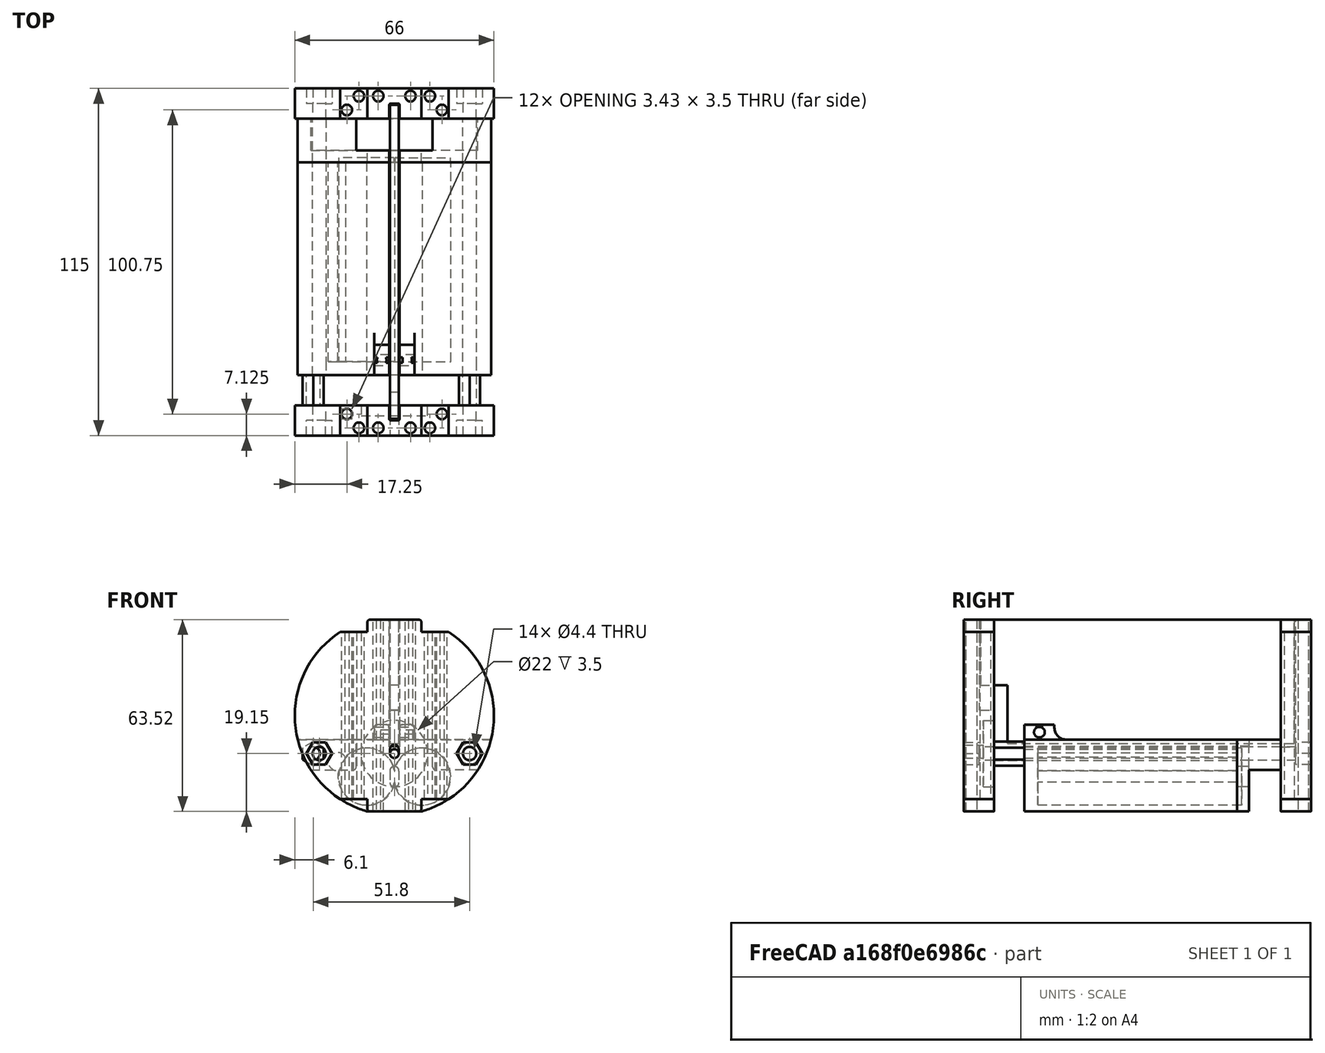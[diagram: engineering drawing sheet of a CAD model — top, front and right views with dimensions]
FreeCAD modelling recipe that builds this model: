
FCSTD DOCUMENT  (FreeCAD 0.19R24276 (Git))
Label: Corte_piezas_DEF_2
License: Creative Commons Attribution-ShareAlike
LicenseURL: http://creativecommons.org/licenses/by-sa/4.0/
objects: Sketcher::SketchObject×22, PartDesign::Pocket×12, PartDesign::Pad×10, TechDraw::DrawViewDimension×9, PartDesign::Fillet×8, PartDesign::Body×7, PartDesign::ShapeBinder×6, PartDesign::Mirrored×5, TechDraw::DrawSVGTemplate×2, TechDraw::DrawViewPart×2, TechDraw::DrawPage×2, Spreadsheet::Sheet×1, PartDesign::MultiTransform×1
note: 101 computed .brp shape members not serialized (recipe doc carries the construction recipe); baked Part::Feature solids carry a one-line shape summary decoded from their .brp

FEATURE [Spreadsheet::Sheet] Spreadsheet  label="Datos"
  cells = A1=Diámetro pila; B1(DiametroPila)=18.5; A2=Tolerancia; B2(tolerancia)=0.4; A3=Largo Pila; B3(largoPila)=65; A4=Separacion; B4(separacion)=1; A5=Grosor tapa; B5(grosortapa)=4.5; A6=Largo Bote; B6(LargoBote)=115; A7= Rosca pasante Diámetro; B7(roscaPasante4)=4; A8=Ancho placa electrónica; B8(anchoPlaca)=3; A9=Diámetro tornillos placa; B9(tornillosParaLaPlaca)=3
FEATURE [Sketcher::SketchObject] Sketch  label="habitaculo_pila_antena"
  FullyConstrained = true
  MapMode = 5
  Placement = pos=(0,0,0) rot=(1,0,0;1.5708rad)
  Support = -> [XZ_Plane]
  expr: Constraints[15] = <<Datos>>.DiametroPila
  expr: Constraints[2] = <<Datos>>.DiametroPila + <<Datos>>.tolerancia
  expr: Constraints[7] = <<Datos>>.tolerancia + <<Datos>>.roscaPasante4
  sketch-geometry (13):
    g0: Circle CenterX=0 CenterY=0 CenterZ=0 NormalX=0 NormalY=0 NormalZ=1 AngleXU=0 Radius=33
    g1: LineSegment StartX=-9.25 StartY=-31.6771 StartZ=0 EndX=9.25 EndY=-31.6771 EndZ=0
    g2: LineSegment StartX=-32.0156 StartY=-8 StartZ=0 EndX=32.0156 EndY=-8 EndZ=0
    g3: ArcOfCircle CenterX=-9.25 CenterY=-20.1771 CenterZ=0 NormalX=0 NormalY=0 NormalZ=1 AngleXU=0 Radius=9.45 StartAngle=0.206102 EndAngle=2.40475
    g4: ArcOfCircle CenterX=9.25 CenterY=-20.1771 CenterZ=0 NormalX=0 NormalY=0 NormalZ=1 AngleXU=0 Radius=9.45 StartAngle=3.3477 EndAngle=9.21868
    g5: Circle CenterX=24.9 CenterY=-12.6 CenterZ=0 NormalX=0 NormalY=0 NormalZ=1 AngleXU=0 Radius=2.2
    g6: ArcOfCircle CenterX=0 CenterY=0 CenterZ=0 NormalX=0 NormalY=0 NormalZ=1 AngleXU=0 Radius=33 StartAngle=3.38646 EndAngle=4.42828
    g7: ArcOfCircle CenterX=0 CenterY=0 CenterZ=0 NormalX=0 NormalY=0 NormalZ=1 AngleXU=0 Radius=33 StartAngle=4.9965 EndAngle=6.03832
    g8: ArcOfCircle CenterX=-18.8935 CenterY=-15.243 CenterZ=0 NormalX=0 NormalY=0 NormalZ=1 AngleXU=0 Radius=3 StartAngle=0.491509 EndAngle=4.84582
    g9: ArcOfCircle CenterX=-9.25 CenterY=-20.1771 CenterZ=0 NormalX=0 NormalY=0 NormalZ=1 AngleXU=0 Radius=9.45 StartAngle=2.93258 EndAngle=6.07708
    g10: Circle CenterX=-24.9 CenterY=-12.6 CenterZ=0 NormalX=0 NormalY=0 NormalZ=1 AngleXU=0 Radius=2.2
    g11: Circle CenterX=0 CenterY=-12.6 CenterZ=0 NormalX=0 NormalY=0 NormalZ=1 AngleXU=0 Radius=1.45
    g12: LineSegment StartX=24.9 StartY=-12.6 StartZ=0 EndX=0 EndY=-12.6 EndZ=0
  constraints (38):
    c: Diameter(g0) = 66
    c: Horizontal(g1)
    c: Diameter(g3) = 18.9
    c: Equal(g3,g4)
    c: Coincident(g4,g9)
    c: Coincident(g4,g3)
    c: Coincident(g0,g-1)
    c: Diameter(g5) = 4.4
    c: Horizontal(g2)
    c: Vertical(g1,g4)
    c: Coincident(g6,g-1)
    c: Coincident(g6,g1)
    c: Coincident(g7,g6)
    c: Coincident(g7,g1)
    c: Symmetric(g4,g3,g-2)
    c: DistanceX(g3,g4) = 18.5
    c: PointOnObject(g1,g0)
    c: DistanceY(g1,g3) = 11.5
    c: DistanceY(g2,g6) = 8
    c: PointOnObject(g6,g0)
    c: Coincident(g2,g6)
    c: Coincident(g7,g2)
    c: Equal(g3,g9)
    c: Coincident(g3,g8)
    c: Coincident(g9,g8)
    c: Coincident(g3,g9)
    c: Radius(g8) = 3
    c: DistanceX(g8,g2) = -13.1222
    c: DistanceY(g8,g2) = 7.24297
    c: Symmetric(g10,g5,g-2)
    c: Equal(g10,g5)
    c: Diameter(g11) = 2.9  'Antena'
    c: Coincident(g12,g5)
    c: Coincident(g12,g11)
    c: Horizontal(g12)
    c: PointOnObject(g11,g-2)
    c: DistanceY(g5,g2) = 4.6
    c: DistanceX(g11,g5) = 24.9
FEATURE [PartDesign::Pad] Pad  label="habitaculo_Pila"
  Direction = (1,1,1)
  Length = 66
  Length2 = 100
  Midplane = true
  Placement = pos=(0,0,0) rot=(1,0,0;1.5708rad)
  Profile = -> Sketch
  Type = 0
  expr: Length = <<Datos>>.largoPila + <<Datos>>.separacion
FEATURE [PartDesign::ShapeBinder] ShapeBinder003
  Placement = pos=(0,-4.5,-1e-15) rot=(0,0,1;0rad)
  TraceSupport = false
FEATURE [Sketcher::SketchObject] Sketch022  label="Sketch_placa"
  ExternalGeometry = -> [ShapeBinder003]
  FullyConstrained = false
  Placement = pos=(0,0,-3.7e-14) rot=(0,0.707107,0.707107;3.14159rad)
  Support = -> [ShapeBinder003]
  expr: Constraints[8] = <<Datos>>.anchoPlaca
  sketch-geometry (4):
    g0: LineSegment StartX=-1.5 StartY=31.7699 StartZ=0 EndX=1.5 EndY=31.7699 EndZ=0
    g1: LineSegment StartX=1.5 StartY=31.7699 StartZ=0 EndX=1.5 EndY=-9.23007 EndZ=0
    g2: LineSegment StartX=1.5 StartY=-9.23007 StartZ=0 EndX=-1.5 EndY=-9.23007 EndZ=0
    g3: LineSegment StartX=-1.5 StartY=-9.23007 StartZ=0 EndX=-1.5 EndY=31.7699 EndZ=0
  constraints (10):
    c: Coincident(g0,g1)
    c: Coincident(g1,g2)
    c: Coincident(g2,g3)
    c: Coincident(g3,g0)
    c: Horizontal(g2)
    c: Vertical(g1)
    c: Vertical(g3)
    c: Symmetric(g0,g0,g-2)
    c: DistanceX(g0,g0) = 3
    c: DistanceY(g1,g1) = 41
FEATURE [PartDesign::Pad] Pad009  label="Placa_electrónica"
  Direction = (1,1,1)
  Length = 104
  Length2 = 100
  Midplane = true
  Placement = pos=(0,-4.5,-1e-15) rot=(0,0,1;0rad)
  Profile = -> Sketch022
  Type = 0
FEATURE [Sketcher::SketchObject] Sketch023
  ExternalGeometry = -> [Pad009]
  FullyConstrained = true
  MapMode = 5
  Placement = pos=(0,-52,5.17e-14) rot=(1,0,0;1.5708rad)
  Support = -> [Pad009]
  sketch-geometry (4):
    g0: LineSegment StartX=-1.5 StartY=-9.23007 StartZ=0 EndX=1.5 EndY=-9.23007 EndZ=0
    g1: LineSegment StartX=1.5 StartY=-9.23007 StartZ=0 EndX=1.5 EndY=10.0699 EndZ=0
    g2: LineSegment StartX=1.5 StartY=10.0699 StartZ=0 EndX=-1.5 EndY=10.0699 EndZ=0
    g3: LineSegment StartX=-1.5 StartY=10.0699 StartZ=0 EndX=-1.5 EndY=-9.23007 EndZ=0
  constraints (11):
    c: Coincident(g0,g1)
    c: Coincident(g1,g2)
    c: Coincident(g2,g3)
    c: Coincident(g3,g0)
    c: Horizontal(g0)
    c: Horizontal(g2)
    c: Vertical(g1)
    c: Vertical(g3)
    c: Coincident(g0,g-3)
    c: PointOnObject(g1,g-4)
    c: DistanceY(g1,g1) = 19.3
FEATURE [PartDesign::Pocket] Pocket011
  BaseFeature = -> Pad009
  Length = 9
  Length2 = 100
  Placement = pos=(0,-4.5,-1e-15) rot=(0,0,1;0rad)
  Profile = -> Sketch023
  Type = 0
FEATURE [PartDesign::Body] Body003  label="Placa_electronica"
  Group = -> [ShapeBinder003,Sketch022,Pad009,Sketch023,Pocket011]
  Origin = -> Origin003
  Tip = -> Pocket011
FEATURE [PartDesign::ShapeBinder] ShapeBinder
  Placement = pos=(0,-4.5,-1e-15) rot=(0,0,1;0rad)
  TraceSupport = false
FEATURE [Sketcher::SketchObject] Sketch024  label="Forma_pasante1"
  ExternalGeometry = -> [ShapeBinder]
  FullyConstrained = true
  MapMode = 5
  Placement = pos=(0,-37.5,-1.19e-14) rot=(1,0,0;1.5708rad)
  Support = -> [ShapeBinder]
  sketch-geometry (8):
    g0: Circle CenterX=24.9 CenterY=-12.6 CenterZ=0 NormalX=0 NormalY=0 NormalZ=1 AngleXU=0 Radius=2.2
    g1: LineSegment StartX=28.3641 StartY=-14.6 StartZ=0 EndX=28.3641 EndY=-10.6 EndZ=0
    g2: LineSegment StartX=28.3641 StartY=-10.6 StartZ=0 EndX=24.9 EndY=-8.6 EndZ=0
    g3: LineSegment StartX=24.9 StartY=-8.6 StartZ=0 EndX=21.4359 EndY=-10.6 EndZ=0
    g4: LineSegment StartX=21.4359 StartY=-10.6 StartZ=0 EndX=21.4359 EndY=-14.6 EndZ=0
    g5: LineSegment StartX=21.4359 StartY=-14.6 StartZ=0 EndX=24.9 EndY=-16.6 EndZ=0
    g6: LineSegment StartX=24.9 StartY=-16.6 StartZ=0 EndX=28.3641 EndY=-14.6 EndZ=0
    g7: Circle CenterX=24.9 CenterY=-12.6 CenterZ=0 NormalX=0 NormalY=0 NormalZ=1 AngleXU=0 Radius=4
  constraints (18):
    c: Coincident(g0,g-3)
    c: Equal(g0,g-3)
    c: Coincident(g1,g2)
    c: Coincident(g2,g3)
    c: Coincident(g3,g4)
    c: Coincident(g4,g5)
    c: Coincident(g5,g6)
    c: Coincident(g6,g1)
    c: Equal(g1, g2-g6) x5
    c: PointOnObject(g1,g7)
    c: PointOnObject(g2,g7)
    c: PointOnObject(g3,g7)
    c: PointOnObject(g4,g7)
    c: PointOnObject(g5,g7)
    c: PointOnObject(g6,g7)
    c: Coincident(g7,g0)
    c: Vertical(g1)
    c: Distance(g2) = 4
FEATURE [PartDesign::Pad] Pad010
  Direction = (1,1,1)
  Length = 10
  Length2 = 100
  Placement = pos=(0,-4.5,-1e-15) rot=(0,0,1;0rad)
  Profile = -> Sketch024
  Type = 0
FEATURE [PartDesign::Body] Body004  label="Pasante1"
  Group = -> [ShapeBinder,Sketch024,Pad010]
  Origin = -> Origin004
  Tip = -> Pad010
FEATURE [PartDesign::ShapeBinder] ShapeBinder004
  Placement = pos=(0,-10,-2.2e-15) rot=(0,0,1;0rad)
  Support = -> [Pad010]
  TraceSupport = false
FEATURE [Sketcher::SketchObject] Sketch025
  ExternalGeometry = -> [ShapeBinder004]
  FullyConstrained = true
  MapMode = 5
  Placement = pos=(0,-47.5,-2.43e-14) rot=(1,0,0;1.5708rad)
  Support = -> [ShapeBinder004]
  sketch-geometry (8):
    g0: Circle CenterX=24.9 CenterY=-12.6 CenterZ=0 NormalX=0 NormalY=0 NormalZ=1 AngleXU=0 Radius=2.2
    g1: LineSegment StartX=28.3641 StartY=-10.6 StartZ=0 EndX=24.9 EndY=-8.6 EndZ=0
    g2: LineSegment StartX=24.9 StartY=-8.6 StartZ=0 EndX=21.4359 EndY=-10.6 EndZ=0
    g3: LineSegment StartX=21.4359 StartY=-10.6 StartZ=0 EndX=21.4359 EndY=-14.6 EndZ=0
    g4: LineSegment StartX=21.4359 StartY=-14.6 StartZ=0 EndX=24.9 EndY=-16.6 EndZ=0
    g5: LineSegment StartX=24.9 StartY=-16.6 StartZ=0 EndX=28.3641 EndY=-14.6 EndZ=0
    g6: LineSegment StartX=28.3641 StartY=-14.6 StartZ=0 EndX=28.3641 EndY=-10.6 EndZ=0
    g7: Circle CenterX=24.9 CenterY=-12.6 CenterZ=0 NormalX=0 NormalY=0 NormalZ=1 AngleXU=0 Radius=4
  constraints (17):
    c: Coincident(g0,g-5)
    c: PointOnObject(g-4,g0)
    c: Coincident(g1,g2)
    c: Coincident(g2,g3)
    c: Coincident(g3,g4)
    c: Coincident(g4,g5)
    c: Coincident(g5,g6)
    c: Coincident(g6,g1)
    c: Equal(g1, g2-g6) x5
    c: PointOnObject(g1,g7)
    c: PointOnObject(g2,g7)
    c: PointOnObject(g3,g7)
    c: PointOnObject(g4,g7)
    c: PointOnObject(g5,g7)
    c: PointOnObject(g6,g7)
    c: Coincident(g7,g0)
    c: Coincident(g6,g-3)
FEATURE [PartDesign::Pad] Pad011
  Direction = (1,1,1)
  Length = 10
  Length2 = 100
  Placement = pos=(0,-10,-2.2e-15) rot=(0,0,1;0rad)
  Profile = -> Sketch025
  Type = 0
FEATURE [PartDesign::Body] Body005  label="Pasante2"
  Group = -> [ShapeBinder004,Sketch025,Pad011]
  Origin = -> Origin005
  Placement = pos=(-51.8,10,1.8e-15) rot=(0,0,1;0rad)
  Tip = -> Pad011
FEATURE [PartDesign::ShapeBinder] ShapeBinder005
  Placement = pos=(0,-4.5,-1e-15) rot=(0,0,1;0rad)
  TraceSupport = false
FEATURE [Sketcher::SketchObject] Sketch026
  ExternalGeometry = -> [ShapeBinder005]
  FullyConstrained = true
  Placement = pos=(0,-47.5,0) rot=(1,0,0;1.5708rad)
  Support = -> [ShapeBinder005]
  sketch-geometry (26):
    g0: ArcOfCircle CenterX=0 CenterY=0 CenterZ=0 NormalX=0 NormalY=0 NormalZ=1 AngleXU=0 Radius=33 StartAngle=5.28932 EndAngle=7.27705
    g1: LineSegment StartX=-9 StartY=-31.749 StartZ=0 EndX=9 EndY=-31.749 EndZ=0
    g2: LineSegment StartX=-9 StartY=31.749 StartZ=0 EndX=9 EndY=31.749 EndZ=0
    g3: ArcOfCircle CenterX=0 CenterY=0 CenterZ=0 NormalX=0 NormalY=0 NormalZ=1 AngleXU=0 Radius=33 StartAngle=2.14773 EndAngle=4.13546
    g4: ArcOfCircle CenterX=0 CenterY=-12.6 CenterZ=0 NormalX=0 NormalY=0 NormalZ=1 AngleXU=0 Radius=1.45 StartAngle=3.14159 EndAngle=6.28319
    g5: ArcOfCircle CenterX=1e-16 CenterY=-11.15 CenterZ=0 NormalX=0 NormalY=0 NormalZ=1 AngleXU=0 Radius=1.45 StartAngle=0 EndAngle=3.14159
    g6: LineSegment StartX=1.45 StartY=-12.6 StartZ=0 EndX=1.45 EndY=-11.15 EndZ=0
    g7: LineSegment StartX=-1.45 StartY=-12.6 StartZ=0 EndX=-1.45 EndY=-11.15 EndZ=0
    g8: LineSegment StartX=-18 StartY=27.6586 StartZ=0 EndX=-18 EndY=-27.6586 EndZ=0
    g9: LineSegment StartX=18 StartY=27.6586 StartZ=0 EndX=18 EndY=-27.6586 EndZ=0
    g10: LineSegment StartX=27.0362 StartY=-16.3 StartZ=0 EndX=29.1724 EndY=-12.6 EndZ=0
    g11: LineSegment StartX=29.1724 StartY=-12.6 StartZ=0 EndX=27.0362 EndY=-8.9 EndZ=0
    g12: LineSegment StartX=27.0362 StartY=-8.9 StartZ=0 EndX=22.7638 EndY=-8.9 EndZ=0
    g13: LineSegment StartX=22.7638 StartY=-8.9 StartZ=0 EndX=20.6276 EndY=-12.6 EndZ=0
    g14: LineSegment StartX=20.6276 StartY=-12.6 StartZ=0 EndX=22.7638 EndY=-16.3 EndZ=0
    g15: LineSegment StartX=22.7638 StartY=-16.3 StartZ=0 EndX=27.0362 EndY=-16.3 EndZ=0
    g16: Circle CenterX=24.9 CenterY=-12.6 CenterZ=0 NormalX=0 NormalY=0 NormalZ=1 AngleXU=0 Radius=4.27239
    g17: LineSegment StartX=22.7638 StartY=-8.9 StartZ=0 EndX=29.1724 EndY=-12.6 EndZ=0
    g18: LineSegment StartX=-18 StartY=27.6586 StartZ=0 EndX=-9 EndY=27.6586 EndZ=0
    g19: LineSegment StartX=-9 StartY=31.749 StartZ=0 EndX=-9 EndY=27.6586 EndZ=0
    g20: LineSegment StartX=-18 StartY=-27.6586 StartZ=0 EndX=-9 EndY=-27.6586 EndZ=0
    g21: LineSegment StartX=-9 StartY=-31.749 StartZ=0 EndX=-9 EndY=-27.6586 EndZ=0
    g22: LineSegment StartX=9 StartY=31.749 StartZ=0 EndX=9 EndY=27.6586 EndZ=0
    g23: LineSegment StartX=18 StartY=27.6586 StartZ=0 EndX=9 EndY=27.6586 EndZ=0
    g24: LineSegment StartX=9 StartY=-31.749 StartZ=0 EndX=9 EndY=-27.6586 EndZ=0
    g25: LineSegment StartX=18 StartY=-27.6586 StartZ=0 EndX=9 EndY=-27.6586 EndZ=0
  constraints (65):
    c: Coincident(g0,g-1)
    c: Coincident(g1,g-4)
    c: PointOnObject(g2,g0)
    c: Horizontal(g2)
    c: Equal(g0,g3)
    c: Coincident(g0,g3)
    c: Tangent(g4,g7) = 1.5708
    c: Tangent(g4,g6) = -1.5708
    c: Tangent(g6,g5) = -1.5708
    c: Tangent(g7,g5) = 1.5708
    c: Vertical(g6)
    c: Equal(g4,g5)
    c: Coincident(g4,g-6)
    c: PointOnObject(g4,g-6)
    c: PointOnObject(g5,g-6)
    c: Vertical(g8)
    c: Vertical(g9)
    c: Coincident(g10,g11)
    c: Coincident(g11,g12)
    c: Coincident(g12,g13)
    c: Coincident(g13,g14)
    c: Coincident(g14,g15)
    c: Coincident(g15,g10)
    c: Equal(g10, g11-g15) x5
    c: PointOnObject(g10,g16)
    c: PointOnObject(g11,g16)
    c: PointOnObject(g12,g16)
    c: PointOnObject(g13,g16)
    c: PointOnObject(g14,g16)
    c: PointOnObject(g15,g16)
    c: Coincident(g16,g-7)
    c: Coincident(g17,g12)
    c: Coincident(g17,g10)
    c: Distance(g17) = 7.4
    c: Horizontal(g15)
    c: Coincident(g19,g2)
    c: Coincident(g19,g18)
    c: Vertical(g19)
    c: Horizontal(g18)
    c: Coincident(g3,g8)
    c: Coincident(g20,g8)
    c: Coincident(g21,g1)
    c: Coincident(g21,g20)
    c: Vertical(g21)
    c: Horizontal(g20)
    c: Coincident(g3,g8)
    c: Vertical(g22)
    c: Coincident(g23,g9)
    c: Coincident(g23,g22)
    c: Coincident(g24,g1)
    c: Vertical(g24)
    c: Coincident(g25,g9)
    c: Coincident(g25,g24)
    c: Horizontal(g25)
    c: Horizontal(g23)
    c: Coincident(g0,g9)
    c: Coincident(g0,g9)
    c: Equal(g23,g18)
    c: Equal(g20,g25)
    c: Equal(g25,g23)
    c: Coincident(g22,g2)
    c: Coincident(g18,g3)
    c: PointOnObject(g0,g-3)
    c: Coincident(g1,g-3)
    c: DistanceX(g23,g23) = 9
FEATURE [PartDesign::Pad] Pad012  label="Cuerpo_principal"
  Direction = (1,1,1)
  Length = 10
  Length2 = 100
  Placement = pos=(0,-4.5,-1e-15) rot=(0,0,1;0rad)
  Profile = -> Sketch026
  Type = 0
FEATURE [Sketcher::SketchObject] Sketch027
  ExternalGeometry = -> [Pad012]
  FullyConstrained = true
  MapMode = 5
  Placement = pos=(0,-4.5,31.749) rot=(0,0,1;0rad)
  Support = -> [Pad012]
  sketch-geometry (4):
    g0: LineSegment StartX=-1.7 StartY=-48 StartZ=0 EndX=1.7 EndY=-48 EndZ=0
    g1: LineSegment StartX=1.7 StartY=-48 StartZ=0 EndX=1.7 EndY=-43 EndZ=0
    g2: LineSegment StartX=1.7 StartY=-43 StartZ=0 EndX=-1.7 EndY=-43 EndZ=0
    g3: LineSegment StartX=-1.7 StartY=-43 StartZ=0 EndX=-1.7 EndY=-48 EndZ=0
  constraints (11):
    c: Coincident(g0,g1)
    c: Coincident(g1,g2)
    c: Coincident(g2,g3)
    c: Coincident(g3,g0)
    c: Horizontal(g0)
    c: Vertical(g1)
    c: Vertical(g3)
    c: PointOnObject(g1,g-4)
    c: Symmetric(g1,g2,g-2)
    c: DistanceX(g0,g0) = 3.4
    c: DistanceY(g1,g1) = 5
FEATURE [PartDesign::Pocket] Pocket  label="Ranura_placa"
  BaseFeature = -> Pad012
  Length = 30
  Length2 = 100
  Placement = pos=(0,-4.5,-1e-15) rot=(0,0,1;0rad)
  Profile = -> Sketch027
  Type = 0
FEATURE [Sketcher::SketchObject] Sketch028  label="SK_agujeros_pasantes_paracaidas"
  ExternalGeometry = -> [Pocket]
  FullyConstrained = true
  MapMode = 5
  Placement = pos=(0,-4.5,31.749) rot=(0,0,1;0rad)
  Support = -> [Pocket]
  sketch-geometry (14):
    g0: LineSegment StartX=-1.7 StartY=-48 StartZ=0 EndX=-9 EndY=-48 EndZ=0
    g1: LineSegment StartX=-1.7 StartY=-48 StartZ=0 EndX=-9 EndY=-53 EndZ=0
    g2: LineSegment StartX=-6.07487 StartY=-48.75 StartZ=0 EndX=-4.62513 EndY=-48.75 EndZ=0
    g3: ArcOfCircle CenterX=-5.35 CenterY=-50.5 CenterZ=0 NormalX=0 NormalY=0 NormalZ=1 AngleXU=0 Radius=1.75 StartAngle=2.35619 EndAngle=7.06858
    g4: LineSegment StartX=-6.07487 StartY=-48.75 StartZ=0 EndX=-6.58744 EndY=-49.2626 EndZ=0
    g5: LineSegment StartX=-4.11256 StartY=-49.2626 StartZ=0 EndX=-4.62513 EndY=-48.75 EndZ=0
    g6: LineSegment StartX=-6.58744 StartY=-49.2626 StartZ=0 EndX=-4.11256 EndY=-49.2626 EndZ=0
    g7: Circle CenterX=-5.35 CenterY=-50.5 CenterZ=0 NormalX=0 NormalY=0 NormalZ=1 AngleXU=0 Radius=1.75
    g8: LineSegment StartX=4.62513 StartY=-48.75 StartZ=0 EndX=6.07487 EndY=-48.75 EndZ=0
    g9: ArcOfCircle CenterX=5.35 CenterY=-50.5 CenterZ=0 NormalX=0 NormalY=0 NormalZ=1 AngleXU=0 Radius=1.75 StartAngle=2.35619 EndAngle=7.06858
    g10: LineSegment StartX=4.62513 StartY=-48.75 StartZ=0 EndX=4.11256 EndY=-49.2626 EndZ=0
    g11: LineSegment StartX=6.58744 StartY=-49.2626 StartZ=0 EndX=6.07487 EndY=-48.75 EndZ=0
    g12: LineSegment StartX=4.11256 StartY=-49.2626 StartZ=0 EndX=6.58744 EndY=-49.2626 EndZ=0
    g13: Circle CenterX=5.35 CenterY=-50.5 CenterZ=0 NormalX=0 NormalY=0 NormalZ=1 AngleXU=0 Radius=1.75
  constraints (33):
    c: Coincident(g0,g-8)
    c: PointOnObject(g0,g-3)
    c: Horizontal(g0)
    c: Coincident(g1,g0)
    c: Coincident(g1,g-3)
    c: Horizontal(g2)
    c: Coincident(g4,g2)
    c: Coincident(g5,g2)
    c: Coincident(g6,g3)
    c: Horizontal(g6)
    c: Tangent(g4,g3) = -1.5708
    c: Tangent(g5,g3) = -1.5708
    c: Angle(g6,g4) = 0.785398
    c: Diameter(g3) = 3.5
    c: Symmetric(g0,g1,g3)
    c: Coincident(g7,g3)
    c: PointOnObject(g3,g7)
    c: Tangent(g7,g2)
    c: Coincident(g3,g6)
    c: Horizontal(g8)
    c: Coincident(g10,g8)
    c: Coincident(g11,g8)
    c: Coincident(g12,g9)
    c: Horizontal(g12)
    c: Tangent(g10,g9) = -1.5708
    c: Tangent(g11,g9) = -1.5708
    c: Angle(g12,g10) = 0.785398
    c: Equal(g3,g9) = 3.5
    c: Coincident(g13,g9)
    c: PointOnObject(g9,g13)
    c: Tangent(g13,g8)
    c: Coincident(g9,g12)
    c: Symmetric(g9,g3,g-2)
FEATURE [PartDesign::Pocket] Pocket012  label="agujeros_pasantes_paracaidas"
  BaseFeature = -> Pocket
  Length = 5
  Length2 = 100
  Placement = pos=(0,-4.5,-1e-15) rot=(0,0,1;0rad)
  Profile = -> Sketch028
  Type = 1
FEATURE [Sketcher::SketchObject] Sketch029
  ExternalGeometry = -> [Pocket012]
  FullyConstrained = true
  MapMode = 5
  Placement = pos=(0,-47.5,8.5e-15) rot=(0,0.707107,0.707107;3.14159rad)
  Support = -> [Pocket012]
  sketch-geometry (2):
    g0: Circle CenterX=0 CenterY=-12.6 CenterZ=0 NormalX=0 NormalY=0 NormalZ=1 AngleXU=0 Radius=11
    g1: Circle CenterX=0 CenterY=-12.6 CenterZ=0 NormalX=0 NormalY=0 NormalZ=1 AngleXU=0 Radius=4
  constraints (4):
    c: Coincident(g0,g-3)
    c: Diameter(g0) = 22
    c: Coincident(g1,g0)
    c: Diameter(g1) = 8
FEATURE [PartDesign::Pocket] Pocket013  label="Arandela_GND"
  BaseFeature = -> Pocket012
  Length = 3.5
  Length2 = 100
  Placement = pos=(0,-4.5,-1e-15) rot=(0,0,1;0rad)
  Profile = -> Sketch029
  Type = 0
FEATURE [Sketcher::SketchObject] Sketch030
  ExternalGeometry = -> [ShapeBinder005]
  FullyConstrained = true
  MapMode = 5
  Placement = pos=(0,-57.5,1.07e-14) rot=(1,0,0;1.5708rad)
  Support = -> [Pocket013]
  sketch-geometry (15):
    g0: LineSegment StartX=27.0362 StartY=-16.3 StartZ=0 EndX=29.1724 EndY=-12.6 EndZ=0
    g1: LineSegment StartX=29.1724 StartY=-12.6 StartZ=0 EndX=27.0362 EndY=-8.9 EndZ=0
    g2: LineSegment StartX=27.0362 StartY=-8.9 StartZ=0 EndX=22.7638 EndY=-8.9 EndZ=0
    g3: LineSegment StartX=22.7638 StartY=-8.9 StartZ=0 EndX=20.6276 EndY=-12.6 EndZ=0
    g4: LineSegment StartX=20.6276 StartY=-12.6 StartZ=0 EndX=22.7638 EndY=-16.3 EndZ=0
    g5: LineSegment StartX=22.7638 StartY=-16.3 StartZ=0 EndX=27.0362 EndY=-16.3 EndZ=0
    g6: Circle CenterX=24.9 CenterY=-12.6 CenterZ=0 NormalX=0 NormalY=0 NormalZ=1 AngleXU=0 Radius=4.27239
    g7: LineSegment StartX=-22.7638 StartY=-16.3 StartZ=0 EndX=-20.6276 EndY=-12.6 EndZ=0
    g8: LineSegment StartX=-20.6276 StartY=-12.6 StartZ=0 EndX=-22.7638 EndY=-8.9 EndZ=0
    g9: LineSegment StartX=-22.7638 StartY=-8.9 StartZ=0 EndX=-27.0362 EndY=-8.9 EndZ=0
    g10: LineSegment StartX=-27.0362 StartY=-8.9 StartZ=0 EndX=-29.1724 EndY=-12.6 EndZ=0
    g11: LineSegment StartX=-29.1724 StartY=-12.6 StartZ=0 EndX=-27.0362 EndY=-16.3 EndZ=0
    g12: LineSegment StartX=-27.0362 StartY=-16.3 StartZ=0 EndX=-22.7638 EndY=-16.3 EndZ=0
    g13: Circle CenterX=-24.9 CenterY=-12.6 CenterZ=0 NormalX=0 NormalY=0 NormalZ=1 AngleXU=0 Radius=4.27239
    g14: LineSegment StartX=22.7638 StartY=-8.9 StartZ=0 EndX=29.1724 EndY=-12.6 EndZ=0
  constraints (34):
    c: Coincident(g0,g1)
    c: Coincident(g1,g2)
    c: Coincident(g2,g3)
    c: Coincident(g3,g4)
    c: Coincident(g4,g5)
    c: Coincident(g5,g0)
    c: Equal(g0, g1-g5) x5
    c: PointOnObject(g0,g6)
    c: PointOnObject(g1,g6)
    c: PointOnObject(g2,g6)
    c: PointOnObject(g3,g6)
    c: PointOnObject(g4,g6)
    c: PointOnObject(g5,g6)
    c: Coincident(g6,g-3)
    c: Coincident(g7,g8)
    c: Coincident(g8,g9)
    c: Coincident(g9,g10)
    c: Coincident(g10,g11)
    c: Coincident(g11,g12)
    c: Coincident(g12,g7)
    c: Equal(g7, g8-g12) x5
    c: PointOnObject(g7,g13)
    c: PointOnObject(g8,g13)
    c: PointOnObject(g9,g13)
    c: PointOnObject(g10,g13)
    c: PointOnObject(g11,g13)
    c: PointOnObject(g12,g13)
    c: Coincident(g13,g-4)
    c: Coincident(g14,g2)
    c: Distance(g14) = 7.4
    c: Horizontal(g5)
    c: Coincident(g14,g0)
    c: Equal(g2,g9)
    c: Horizontal(g12)
FEATURE [PartDesign::Pocket] Pocket014  label="Encastro_tuercas"
  BaseFeature = -> Pocket013
  Length = 5
  Length2 = 100
  Placement = pos=(0,-4.5,-1e-15) rot=(0,0,1;0rad)
  Profile = -> Sketch030
  Type = 0
FEATURE [Sketcher::SketchObject] Sketch031
  ExternalGeometry = -> [Pocket014]
  FullyConstrained = true
  MapMode = 5
  Placement = pos=(0,-52.5,4.51e-14) rot=(1,0,0;1.5708rad)
  Support = -> [Pocket014]
  sketch-geometry (3):
    g0: Circle CenterX=24.9 CenterY=-12.6 CenterZ=0 NormalX=0 NormalY=0 NormalZ=1 AngleXU=0 Radius=4.27239
    g1: Circle CenterX=24.9 CenterY=-12.6 CenterZ=0 NormalX=0 NormalY=0 NormalZ=1 AngleXU=0 Radius=2.2
    g2: Circle CenterX=-24.9 CenterY=-12.6 CenterZ=0 NormalX=0 NormalY=0 NormalZ=1 AngleXU=0 Radius=2.2
  constraints (7):
    c: PointOnObject(g-8,g0)
    c: PointOnObject(g-4,g0)
    c: PointOnObject(g-5,g0)
    c: Coincident(g1,g0)
    c: Diameter(g1) = 4.4
    c: Equal(g1,g2) = 4.4
    c: Symmetric(g2,g1,g-2)
FEATURE [PartDesign::Pocket] Pocket015  label="Agujeros_pasantes_tornillos"
  BaseFeature = -> Pocket014
  Length = 5
  Length2 = 100
  Placement = pos=(0,-4.5,-1e-15) rot=(0,0,1;0rad)
  Profile = -> Sketch031
  Type = 1
FEATURE [Sketcher::SketchObject] Sketch032  label="SK_agujeros_pasantes_paracaidas_2"
  ExternalGeometry = -> [Pocket015]
  FullyConstrained = true
  MapMode = 5
  Placement = pos=(0,-4.5,27.6586) rot=(0,0,1;0rad)
  Support = -> [Pocket015]
  sketch-geometry (16):
    g0: LineSegment StartX=11.0251 StartY=-48.75 StartZ=0 EndX=12.4749 EndY=-48.75 EndZ=0
    g1: ArcOfCircle CenterX=11.75 CenterY=-50.5 CenterZ=0 NormalX=0 NormalY=0 NormalZ=1 AngleXU=0 Radius=1.75 StartAngle=2.35619 EndAngle=7.06858
    g2: LineSegment StartX=11.0251 StartY=-48.75 StartZ=0 EndX=10.5126 EndY=-49.2626 EndZ=0
    g3: LineSegment StartX=12.4749 StartY=-48.75 StartZ=0 EndX=12.9874 EndY=-49.2626 EndZ=0
    g4: LineSegment StartX=10.5126 StartY=-49.2626 StartZ=0 EndX=12.9874 EndY=-49.2626 EndZ=0
    g5: LineSegment StartX=6.07487 StartY=-48.75 StartZ=0 EndX=18 EndY=-48.75 EndZ=0
    g6: LineSegment StartX=13.5 StartY=-43 StartZ=0 EndX=13.5 EndY=-53 EndZ=0
    g7: ArcOfCircle CenterX=11.75 CenterY=-50.5 CenterZ=0 NormalX=0 NormalY=0 NormalZ=1 AngleXU=0 Radius=1.75 StartAngle=1.5708 EndAngle=2.35619
    g8: LineSegment StartX=15.0251 StartY=-44.125 StartZ=0 EndX=16.4749 EndY=-44.125 EndZ=0
    g9: ArcOfCircle CenterX=15.75 CenterY=-45.875 CenterZ=0 NormalX=0 NormalY=0 NormalZ=1 AngleXU=0 Radius=1.75 StartAngle=2.35619 EndAngle=7.06858
    g10: LineSegment StartX=15.0251 StartY=-44.125 StartZ=0 EndX=14.5126 EndY=-44.6376 EndZ=0
    g11: LineSegment StartX=16.4749 StartY=-44.125 StartZ=0 EndX=16.9874 EndY=-44.6376 EndZ=0
    g12: LineSegment StartX=14.5126 StartY=-44.6376 StartZ=0 EndX=16.9874 EndY=-44.6376 EndZ=0
    g13: ArcOfCircle CenterX=15.75 CenterY=-45.875 CenterZ=0 NormalX=0 NormalY=0 NormalZ=1 AngleXU=0 Radius=1.75 StartAngle=1.57079 EndAngle=2.35619
    g14: LineSegment StartX=13.5 StartY=-43 StartZ=0 EndX=18 EndY=-48.75 EndZ=0
    g15: LineSegment StartX=13.5 StartY=-48.75 StartZ=0 EndX=18 EndY=-43 EndZ=0
  constraints (43):
    c: Diameter(g1) = 3.5
    c: Coincident(g1,g4)
    c: Horizontal(g4)
    c: Coincident(g0,g2)
    c: Horizontal(g0)
    c: Coincident(g0,g3)
    c: PointOnObject(g5,g-3)
    c: Horizontal(g5)
    c: PointOnObject(g6,g-5)
    c: Vertical(g6)
    c: Symmetric(g-4,g-6,g6)
    c: Tangent(g1,g2) = -1.5708
    c: Tangent(g3,g1) = 1.5708
    c: Coincident(g4,g1)
    c: Coincident(g7,g1)
    c: Coincident(g7,g1)
    c: Tangent(g0,g7)
    c: Angle(g4,g2) = 0.785398
    c: PointOnObject(g7,g0)
    c: Coincident(g5,g-7)
    c: Diameter(g9) = 3.5
    c: Coincident(g9,g12)
    c: Horizontal(g12)
    c: Coincident(g8,g10)
    c: Horizontal(g8)
    c: Coincident(g8,g11)
    c: Tangent(g9,g10) = -1.5708
    c: Tangent(g11,g9) = 1.5708
    c: Coincident(g12,g9)
    c: Coincident(g13,g9)
    c: Coincident(g13,g9)
    c: Tangent(g8,g13)
    c: Angle(g12,g10) = 0.785398
    c: PointOnObject(g13,g8)
    c: Coincident(g14,g6)
    c: Coincident(g14,g5)
    c: PointOnObject(g9,g14)
    c: PointOnObject(g15,g6)
    c: Coincident(g15,g-4)
    c: PointOnObject(g9,g15)
    c: PointOnObject(g15,g5)
    c: PointOnObject(g0,g5)
    c: Tangent(g1,g6)
FEATURE [PartDesign::Pocket] Pocket016  label="Agujeros_pasantes_paracaidas_2"
  BaseFeature = -> Pocket015
  Length = 5
  Length2 = 100
  Placement = pos=(0,-4.5,-1e-15) rot=(0,0,1;0rad)
  Profile = -> Sketch032
  Type = 1
FEATURE [PartDesign::Mirrored] Mirrored  label="Con_todos_agujeros_pasantes"
  BaseFeature = -> Pocket016
  MirrorPlane = -> Sketch032 [V_Axis]
  Originals = -> [Pocket016]
  Placement = pos=(0,-4.5,-1e-15) rot=(0,0,1;0rad)
FEATURE [PartDesign::Fillet] Fillet
  Base = -> Mirrored [Edge123,Edge109]
  BaseFeature = -> Mirrored
  Placement = pos=(0,-4.5,-1e-15) rot=(0,0,1;0rad)
  Radius = 0.5
  SupportTransform = false
FEATURE [PartDesign::Fillet] Fillet001
  Base = -> Fillet [Edge5,Edge9]
  BaseFeature = -> Fillet
  Placement = pos=(0,-4.5,-1e-15) rot=(0,0,1;0rad)
  Radius = 1
  SupportTransform = false
FEATURE [PartDesign::Fillet] Fillet002
  Base = -> Fillet001 [Edge114,Edge115]
  BaseFeature = -> Fillet001
  Placement = pos=(0,-4.5,-1e-15) rot=(0,0,1;0rad)
  Radius = 1
  SupportTransform = false
FEATURE [PartDesign::Body] Body006  label="LateralA"
  Group = -> [ShapeBinder005,Sketch026,Pad012,Sketch027,Pocket,Sketch028,Pocket012,Sketch029,Pocket013,Sketch030,Pocket014,Sketch031,Pocket015,Sketch032,Pocket016,Mirrored,Fillet,Fillet001,Fillet002]
  Origin = -> Origin006
  Tip = -> Fillet002
FEATURE [PartDesign::ShapeBinder] ShapeBinder006
  Placement = pos=(0,33,7e-15) rot=(0,0,1;0rad)
  TraceSupport = false
FEATURE [Sketcher::SketchObject] Sketch033
  ExternalGeometry = -> [ShapeBinder006]
  FullyConstrained = true
  MapMode = 5
  Placement = pos=(0,33,7e-15) rot=(0,0.707107,0.707107;3.14159rad)
  Support = -> [ShapeBinder006]
  sketch-geometry (10):
    g0: ArcOfCircle CenterX=1.2e-15 CenterY=0 CenterZ=0 NormalX=0 NormalY=0 NormalZ=1 AngleXU=0 Radius=33 StartAngle=4.98862 EndAngle=6.03832
    g1: ArcOfCircle CenterX=1.2e-15 CenterY=0 CenterZ=0 NormalX=0 NormalY=0 NormalZ=1 AngleXU=0 Radius=33 StartAngle=3.38646 EndAngle=4.43616
    g2: LineSegment StartX=-32.0156 StartY=-8 StartZ=0 EndX=32.0156 EndY=-8 EndZ=0
    g3: LineSegment StartX=9 StartY=-31.749 StartZ=0 EndX=-9 EndY=-31.749 EndZ=0
    g4: ArcOfCircle CenterX=0 CenterY=-18.3411 CenterZ=0 NormalX=0 NormalY=0 NormalZ=1 AngleXU=0 Radius=1.5 StartAngle=9e-16 EndAngle=3.14159
    g5: ArcOfCircle CenterX=0 CenterY=-22.1569 CenterZ=0 NormalX=0 NormalY=0 NormalZ=1 AngleXU=0 Radius=1.5 StartAngle=3.14159 EndAngle=6.28319
    g6: LineSegment StartX=-1.5 StartY=-18.3411 StartZ=0 EndX=-1.5 EndY=-22.1569 EndZ=0
    g7: LineSegment StartX=1.5 StartY=-18.3411 StartZ=0 EndX=1.5 EndY=-22.1569 EndZ=0
    g8: Circle CenterX=24.9 CenterY=-12.6 CenterZ=0 NormalX=0 NormalY=0 NormalZ=1 AngleXU=0 Radius=2.2
    g9: Circle CenterX=-24.9 CenterY=-12.6 CenterZ=0 NormalX=0 NormalY=0 NormalZ=1 AngleXU=0 Radius=2.2
  constraints (21):
    c: Coincident(g0,g-3)
    c: Coincident(g0,g-4)
    c: Coincident(g1,g0)
    c: Coincident(g1,g-3)
    c: Coincident(g1,g-4)
    c: Coincident(g2,g1)
    c: Coincident(g2,g0)
    c: Coincident(g3,g0)
    c: Coincident(g3,g1)
    c: Tangent(g4,g7) = 1.5708
    c: Tangent(g4,g6) = -1.5708
    c: Tangent(g6,g5) = -1.5708
    c: Tangent(g7,g5) = 1.5708
    c: Vertical(g6)
    c: Coincident(g4,g-5)
    c: Coincident(g5,g-6)
    c: Diameter(g4) = 3
    c: Coincident(g8,g-8)
    c: Equal(g8,g-7)
    c: Coincident(g9,g-7)
    c: Equal(g9,g-7)
FEATURE [PartDesign::Pad] Pad013  label="tapa_pilas"
  Direction = (1,1,1)
  Length = 4
  Length2 = 100
  Placement = pos=(0,33,7e-15) rot=(0,0,1;0rad)
  Profile = -> Sketch033
  Type = 0
FEATURE [Sketcher::SketchObject] Sketch034
  ExternalGeometry = -> [Pad013]
  FullyConstrained = true
  MapMode = 5
  Placement = pos=(0,37,8.3e-15) rot=(0,0.707107,0.707107;3.14159rad)
  Support = -> [Pad013]
  sketch-geometry (10):
    g0: ArcOfCircle CenterX=0 CenterY=0 CenterZ=0 NormalX=0 NormalY=0 NormalZ=1 AngleXU=0 Radius=33 StartAngle=3.38646 EndAngle=3.71852
    g1: LineSegment StartX=-27.6586 StartY=-18 StartZ=0 EndX=-12.6586 EndY=-18 EndZ=0
    g2: LineSegment StartX=-12.6586 StartY=-18 StartZ=0 EndX=-12.6586 EndY=-8 EndZ=0
    g3: LineSegment StartX=-32.0156 StartY=-8 StartZ=0 EndX=-12.6586 EndY=-8 EndZ=0
    g4: Circle CenterX=-24.9 CenterY=-12.6 CenterZ=0 NormalX=0 NormalY=0 NormalZ=1 AngleXU=0 Radius=2.2
    g5: ArcOfCircle CenterX=-5.1e-15 CenterY=-8.1e-15 CenterZ=0 NormalX=0 NormalY=0 NormalZ=1 AngleXU=0 Radius=33 StartAngle=5.70625 EndAngle=6.03832
    g6: LineSegment StartX=27.6586 StartY=-18 StartZ=0 EndX=12.6586 EndY=-18 EndZ=0
    g7: LineSegment StartX=12.6586 StartY=-18 StartZ=0 EndX=12.6586 EndY=-8 EndZ=0
    g8: LineSegment StartX=32.0156 StartY=-8 StartZ=0 EndX=12.6586 EndY=-8 EndZ=0
    g9: Circle CenterX=24.9 CenterY=-12.6 CenterZ=0 NormalX=0 NormalY=0 NormalZ=1 AngleXU=0 Radius=2.2
  constraints (24):
    c: Coincident(g0,g-1)
    c: Coincident(g0,g-3)
    c: Coincident(g1,g0)
    c: Horizontal(g1)
    c: PointOnObject(g2,g-3)
    c: Vertical(g2)
    c: Coincident(g2,g1)
    c: Coincident(g3,g0)
    c: Coincident(g3,g2)
    c: DistanceY(g2,g2) = 10
    c: DistanceX(g1,g1) = 15
    c: Coincident(g4,g-4)
    c: Equal(g-4,g4)
    c: Coincident(g6,g5)
    c: Coincident(g7,g6)
    c: Coincident(g8,g5)
    c: Coincident(g8,g7)
    c: Symmetric(g7,g2,g-2)
    c: Symmetric(g6,g1,g-2)
    c: Symmetric(g5,g0,g-2)
    c: Symmetric(g9,g4,g-2)
    c: Equal(g9,g4)
    c: Equal(g5,g0)
    c: Symmetric(g5,g0,g-2)
FEATURE [PartDesign::Pad] Pad014
  BaseFeature = -> Pad013
  Direction = (1,1,1)
  Length = 10.5
  Length2 = 100
  Placement = pos=(0,33,7e-15) rot=(0,0,1;0rad)
  Profile = -> Sketch034
  Type = 0
FEATURE [PartDesign::Fillet] Fillet003
  Base = -> Pad014 [Edge51,Edge48]
  BaseFeature = -> Pad014
  Placement = pos=(0,33,7e-15) rot=(0,0,1;0rad)
  Radius = 1
  SupportTransform = false
FEATURE [PartDesign::ShapeBinder] ShapeBinder007
  TraceSupport = false
FEATURE [Sketcher::SketchObject] Sketch035
  ExternalGeometry = -> [ShapeBinder007]
  FullyConstrained = true
  MapMode = 5
  Placement = pos=(0,-47.5,1.04e-14) rot=(0,0.707107,0.707107;3.14159rad)
  Support = -> [ShapeBinder007]
  sketch-geometry (14):
    g0: ArcOfCircle CenterX=0 CenterY=-1.2e-14 CenterZ=0 NormalX=0 NormalY=0 NormalZ=1 AngleXU=0 Radius=33 StartAngle=2.14773 EndAngle=4.13546
    g1: ArcOfCircle CenterX=0 CenterY=-1.2e-14 CenterZ=0 NormalX=0 NormalY=0 NormalZ=1 AngleXU=0 Radius=33 StartAngle=5.28932 EndAngle=7.27705
    g2: LineSegment StartX=-18 StartY=27.6586 StartZ=0 EndX=-9 EndY=27.6586 EndZ=0
    g3: LineSegment StartX=9 StartY=27.6586 StartZ=0 EndX=18 EndY=27.6586 EndZ=0
    g4: LineSegment StartX=-9 StartY=27.6586 StartZ=0 EndX=-9 EndY=31.749 EndZ=0
    g5: LineSegment StartX=9 StartY=27.6586 StartZ=0 EndX=9 EndY=31.749 EndZ=0
    g6: LineSegment StartX=-9 StartY=31.749 StartZ=0 EndX=9 EndY=31.749 EndZ=0
    g7: LineSegment StartX=-9 StartY=-27.6586 StartZ=0 EndX=-9 EndY=-31.749 EndZ=0
    g8: LineSegment StartX=9 StartY=-27.6586 StartZ=0 EndX=9 EndY=-31.749 EndZ=0
    g9: LineSegment StartX=9 StartY=-27.6586 StartZ=0 EndX=18 EndY=-27.6586 EndZ=0
    g10: LineSegment StartX=-18 StartY=-27.6586 StartZ=0 EndX=-9 EndY=-27.6586 EndZ=0
    g11: LineSegment StartX=-9 StartY=-31.749 StartZ=0 EndX=9 EndY=-31.749 EndZ=0
    g12: Circle CenterX=-24.9 CenterY=-12.6 CenterZ=0 NormalX=0 NormalY=0 NormalZ=1 AngleXU=0 Radius=2.2
    g13: Circle CenterX=24.9 CenterY=-12.6 CenterZ=0 NormalX=0 NormalY=0 NormalZ=1 AngleXU=0 Radius=2.2
  constraints (34):
    c: Coincident(g0,g-5)
    c: Coincident(g0,g-7)
    c: Coincident(g1,g0)
    c: Coincident(g1,g-6)
    c: Coincident(g1,g-9)
    c: Coincident(g2,g0)
    c: Coincident(g2,g-5)
    c: Coincident(g3,g-6)
    c: Coincident(g3,g1)
    c: Coincident(g4,g2)
    c: Vertical(g4)
    c: Coincident(g5,g3)
    c: Vertical(g5)
    c: Coincident(g6,g4)
    c: Coincident(g6,g5)
    c: Horizontal(g6)
    c: PointOnObject(g-3,g6)
    c: Coincident(g7,g-7)
    c: Vertical(g7)
    c: Coincident(g8,g-9)
    c: Vertical(g8)
    c: Coincident(g9,g8)
    c: Coincident(g9,g1)
    c: Coincident(g10,g0)
    c: Coincident(g10,g7)
    c: Coincident(g11,g7)
    c: Coincident(g11,g8)
    c: Horizontal(g11)
    c: PointOnObject(g-8,g11)
    c: Coincident(g12,g-10)
    c: Coincident(g13,g-11)
    c: Equal(g12,g13)
    c: Equal(g13,g-11)
    c: Coincident(g0,g-1)
FEATURE [PartDesign::Pad] Pad015
  Direction = (1,1,1)
  Length = 10
  Length2 = 100
  Profile = -> Sketch035
  Reversed = true
  Type = 0
FEATURE [Sketcher::SketchObject] Sketch036
  ExternalGeometry = -> [Pad015]
  FullyConstrained = true
  MapMode = 5
  Placement = pos=(0,-47.5,1.04e-14) rot=(0,0.707107,0.707107;3.14159rad)
  Support = -> [Pad015]
  sketch-geometry (4):
    g0: LineSegment StartX=-1.7 StartY=31.749 StartZ=0 EndX=1.7 EndY=31.749 EndZ=0
    g1: LineSegment StartX=1.7 StartY=31.749 StartZ=0 EndX=1.7 EndY=-10.351 EndZ=0
    g2: LineSegment StartX=1.7 StartY=-10.351 StartZ=0 EndX=-1.7 EndY=-10.351 EndZ=0
    g3: LineSegment StartX=-1.7 StartY=-10.351 StartZ=0 EndX=-1.7 EndY=31.749 EndZ=0
  constraints (11):
    c: Coincident(g0,g1)
    c: Coincident(g1,g2)
    c: Coincident(g2,g3)
    c: Coincident(g3,g0)
    c: Horizontal(g2)
    c: Vertical(g1)
    c: Vertical(g3)
    c: PointOnObject(g0,g-3)
    c: Symmetric(g0,g0,g-2)
    c: DistanceX(g0,g0) = 3.4
    c: DistanceY(g1,g1) = 42.1
FEATURE [PartDesign::Pocket] Pocket017
  BaseFeature = -> Pad015
  Length = 5
  Length2 = 100
  Profile = -> Sketch036
  Type = 0
FEATURE [PartDesign::Mirrored] Mirrored001
  BaseFeature = -> Pocket017
  MirrorPlane = -> Sketch028 [V_Axis]
  Originals = -> [Pocket012]
FEATURE [PartDesign::Mirrored] Mirrored002
  MirrorPlane = -> Sketch032 [V_Axis]
FEATURE [PartDesign::Mirrored] Mirrored003
  MirrorPlane = -> Sketch032 [V_Axis]
FEATURE [PartDesign::MultiTransform] MultiTransform
  BaseFeature = -> Mirrored001
  Originals = -> [Pocket016]
  Transformations = -> [Mirrored002,Mirrored003]
FEATURE [PartDesign::Mirrored] Mirrored004
  BaseFeature = -> MultiTransform
  MirrorPlane = -> Sketch030 [V_Axis]
  Originals = -> [Pocket014]
FEATURE [PartDesign::Fillet] Fillet004
  Base = -> Mirrored004 [Edge85,Edge88]
  BaseFeature = -> Mirrored004
  Radius = 0.5
  SupportTransform = false
FEATURE [PartDesign::Fillet] Fillet005
  Base = -> Fillet004 [Edge9,Edge5,Edge113,Edge114]
  BaseFeature = -> Fillet004
  Radius = 1
  SupportTransform = false
FEATURE [PartDesign::Body] Body009  label="LateralB"
  Group = -> [ShapeBinder007,Sketch035,Pad015,Sketch036,Pocket017,Mirrored001,MultiTransform,Mirrored002,Mirrored003,Mirrored004,Fillet004,Fillet005]
  Origin = -> Origin009
  Placement = pos=(0,0,0) rot=(0,0,1;3.14159rad)
  Tip = -> Fillet005
FEATURE [TechDraw::DrawSVGTemplate] Template
  EditableTexts = Designed_by_Name=Designed by Name; Drawing_number=Drawing number; FC-Date=Date; FC-SC=Scale; FC-SH=Sheet; FC-Title=Title; Subtitle=Subtitle; Weight=Weight
  Height = 210
  Orientation = 1
  Width = 297
FEATURE [TechDraw::DrawSVGTemplate] Template001
  EditableTexts = Designed_by_Name=Designed by Name; Drawing_number=Drawing number; FC-Date=Date; FC-SC=Scale; FC-SH=Sheet; FC-Title=Title; Subtitle=Subtitle; Weight=Weight
  Height = 210
  Orientation = 1
  Width = 297
FEATURE [TechDraw::DrawViewPart] View001
  CoarseView = false
  Direction = (1,0,0)
  Focus = 100
  HardHidden = false
  IsoCount = 0
  IsoHidden = false
  IsoVisible = false
  LockPosition = false
  Perspective = false
  Rotation = 0
  Scale = 2
  ScaleType = 0
  SeamHidden = false
  SeamVisible = true
  SmoothHidden = false
  SmoothVisible = true
  Source = -> [Body003]
  X = 147.843
  XDirection = (0,1,0)
  Y = 132.277
FEATURE [TechDraw::DrawViewDimension] Dimension004
  Arbitrary = false
  ArbitraryTolerances = false
  EqualTolerance = true
  FormatSpec = %.2f
  FormatSpecOverTolerance = %+.2f
  FormatSpecUnderTolerance = %+.2f
  Inverted = false
  LockPosition = false
  MeasureType = 1
  OverTolerance = 0
  References2D = -> [View001]
  Rotation = 0
  ScaleType = 0
  TheoreticalExact = false
  Type = 1
  UnderTolerance = 0
  X = 0
  Y = 53.2239
FEATURE [TechDraw::DrawViewDimension] Dimension005
  Arbitrary = false
  ArbitraryTolerances = false
  EqualTolerance = true
  FormatSpec = %.2f
  FormatSpecOverTolerance = %+.2f
  FormatSpecUnderTolerance = %+.2f
  Inverted = false
  LockPosition = false
  MeasureType = 1
  OverTolerance = 0
  References2D = -> [View001]
  Rotation = 0
  ScaleType = 0
  TheoreticalExact = false
  Type = 2
  UnderTolerance = 0
  X = 113.202
  Y = 0
FEATURE [TechDraw::DrawViewDimension] Dimension006
  Arbitrary = false
  ArbitraryTolerances = false
  EqualTolerance = true
  FormatSpec = %.2f
  FormatSpecOverTolerance = %+.2f
  FormatSpecUnderTolerance = %+.2f
  Inverted = false
  LockPosition = false
  MeasureType = 1
  OverTolerance = 0
  References2D = -> [View001]
  Rotation = 0
  ScaleType = 0
  TheoreticalExact = false
  Type = 1
  UnderTolerance = 0
  X = -119.319
  Y = -43.8728
FEATURE [TechDraw::DrawViewDimension] Dimension007
  Arbitrary = false
  ArbitraryTolerances = false
  EqualTolerance = true
  FormatSpec = %.2f
  FormatSpecOverTolerance = %+.2f
  FormatSpecUnderTolerance = %+.2f
  Inverted = false
  LockPosition = false
  MeasureType = 1
  OverTolerance = 0
  References2D = -> [View001]
  Rotation = 0
  ScaleType = 0
  TheoreticalExact = false
  Type = 2
  UnderTolerance = 0
  X = -125.437
  Y = -17.8207
FEATURE [TechDraw::DrawViewDimension] Dimension008
  Arbitrary = false
  ArbitraryTolerances = false
  EqualTolerance = true
  FormatSpec = %.2f
  FormatSpecOverTolerance = %+.2f
  FormatSpecUnderTolerance = %+.2f
  Inverted = false
  LockPosition = false
  MeasureType = 1
  OverTolerance = 0
  References2D = -> [View001]
  Rotation = 0
  ScaleType = 0
  TheoreticalExact = false
  Type = 2
  UnderTolerance = 0
  X = -125.362
  Y = 19.3
FEATURE [TechDraw::DrawPage] Page001  label="Placa_electrónica_vista"
  KeepUpdated = true
  NextBalloonIndex = 1
  ProjectionType = 0
  Template = -> Template001
  Views = -> [View001,Dimension004,Dimension005,Dimension006,Dimension007,Dimension008]
FEATURE [Sketcher::SketchObject] Sketch037
  ExternalGeometry = -> [Pad]
  FullyConstrained = true
  MapMode = 5
  Placement = pos=(0,-33,-7.3e-15) rot=(1,0,0;1.5708rad)
  Support = -> [Pad]
  sketch-geometry (7):
    g0: ArcOfCircle CenterX=-7e-16 CenterY=2.8e-15 CenterZ=0 NormalX=0 NormalY=0 NormalZ=1 AngleXU=0 Radius=33 StartAngle=3.38646 EndAngle=4.42828
    g1: ArcOfCircle CenterX=-7e-16 CenterY=2.8e-15 CenterZ=0 NormalX=0 NormalY=0 NormalZ=1 AngleXU=0 Radius=33 StartAngle=4.9965 EndAngle=6.03832
    g2: LineSegment StartX=-32.0156 StartY=-8 StartZ=0 EndX=32.0156 EndY=-8 EndZ=0
    g3: LineSegment StartX=9.25 StartY=-31.6771 StartZ=0 EndX=-9.25 EndY=-31.6771 EndZ=0
    g4: Circle CenterX=-24.9 CenterY=-12.6 CenterZ=0 NormalX=0 NormalY=0 NormalZ=1 AngleXU=0 Radius=2.2
    g5: Circle CenterX=0 CenterY=-12.6 CenterZ=0 NormalX=0 NormalY=0 NormalZ=1 AngleXU=0 Radius=1.45
    g6: Circle CenterX=24.9 CenterY=-12.6 CenterZ=0 NormalX=0 NormalY=0 NormalZ=1 AngleXU=0 Radius=2.2
  constraints (15):
    c: Coincident(g0,g-3)
    c: Coincident(g0,g-4)
    c: Coincident(g1,g0)
    c: Coincident(g1,g-3)
    c: Coincident(g1,g-4)
    c: Coincident(g2,g0)
    c: Coincident(g2,g1)
    c: Coincident(g3,g1)
    c: Coincident(g3,g0)
    c: Coincident(g4,g-5)
    c: Coincident(g5,g-7)
    c: Coincident(g6,g-6)
    c: Equal(g6,g-6)
    c: Equal(g5,g-7)
    c: Equal(g4,g-5)
FEATURE [PartDesign::Pad] Pad016  label="Tapa_Habitaculo_pieza"
  BaseFeature = -> Pad
  Direction = (1,1,1)
  Length = 4.5
  Length2 = 100
  Placement = pos=(0,0,0) rot=(1,0,0;1.5708rad)
  Profile = -> Sketch037
  Type = 0
  expr: Length = <<Datos>>.grosortapa
FEATURE [Sketcher::SketchObject] Sketch039
  FullyConstrained = false
  MapMode = 5
  Placement = pos=(0,2e-15,-8) rot=(0,0,1;3.14159rad)
  expr: Constraints[7] = <<Datos>>.anchoPlaca + <<Datos>>.tolerancia + 2 * 5
  sketch-geometry (4):
    g0: LineSegment StartX=-6.7 StartY=37.5 StartZ=0 EndX=6.7 EndY=37.5 EndZ=0
    g1: LineSegment StartX=6.7 StartY=37.5 StartZ=0 EndX=6.7 EndY=27.5 EndZ=0
    g2: LineSegment StartX=6.7 StartY=27.5 StartZ=0 EndX=-6.7 EndY=27.5 EndZ=0
    g3: LineSegment StartX=-6.7 StartY=27.5 StartZ=0 EndX=-6.7 EndY=37.5 EndZ=0
  constraints (10):
    c: Coincident(g0,g1)
    c: Coincident(g1,g2)
    c: Coincident(g2,g3)
    c: Coincident(g3,g0)
    c: Horizontal(g2)
    c: Vertical(g1)
    c: Vertical(g3)
    c: DistanceX(g0,g0) = 13.4
    c: DistanceY(g3,g3) = 10
    c: Symmetric(g0,g0,g-2)
FEATURE [PartDesign::Pad] Pad017  label="bloque_taladro"
  BaseFeature = -> Pad016
  Direction = (1,1,1)
  Length = 5
  Length2 = 100
  Placement = pos=(0,0,0) rot=(1,0,0;1.5708rad)
  Profile = -> Sketch039
  Type = 0
FEATURE [Sketcher::SketchObject] Sketch040  label="SK_taladro_placa"
  ExternalGeometry = -> [Pad017]
  FullyConstrained = false
  MapMode = 5
  Placement = pos=(6.7,0,0) rot=(0.707107,0,0.707107;3.14159rad)
  Support = -> [Pad017]
  sketch-geometry (7):
    g0: LineSegment StartX=-8 StartY=37.5 StartZ=0 EndX=-3 EndY=27.5 EndZ=0
    g1: LineSegment StartX=-6.22487 StartY=30.75 StartZ=0 EndX=-4.77513 EndY=30.75 EndZ=0
    g2: LineSegment StartX=-4.77513 StartY=30.75 StartZ=0 EndX=-4.26256 EndY=31.2626 EndZ=0
    g3: LineSegment StartX=-6.22487 StartY=30.75 StartZ=0 EndX=-6.73744 EndY=31.2626 EndZ=0
    g4: LineSegment StartX=-6.73744 StartY=31.2626 StartZ=0 EndX=-4.26256 EndY=31.2626 EndZ=0
    g5: ArcOfCircle CenterX=-5.5 CenterY=32.5 CenterZ=0 NormalX=0 NormalY=0 NormalZ=1 AngleXU=0 Radius=1.75 StartAngle=5.49779 EndAngle=10.2102
    g6: ArcOfCircle CenterX=-5.5 CenterY=32.5 CenterZ=0 NormalX=0 NormalY=0 NormalZ=1 AngleXU=0 Radius=1.75 StartAngle=3.92699 EndAngle=5.49779
  constraints (15):
    c: Horizontal(g1)
    c: Coincident(g2,g1)
    c: Coincident(g3,g1)
    c: Coincident(g4,g3)
    c: Coincident(g4,g2)
    c: Horizontal(g4)
    c: Coincident(g5,g4)
    c: Tangent(g5,g2) = -1.5708
    c: Diameter(g5) = 3.5
    c: Symmetric(g0,g0,g5)
    c: Coincident(g6,g5)
    c: Coincident(g6,g3)
    c: Tangent(g1,g6)
    c: Angle(g4,g2) = 0.785398
    c: Tangent(g3,g5)
FEATURE [PartDesign::Pocket] Pocket018  label="Taladro_placa"
  BaseFeature = -> Pad017
  Length = 5
  Length2 = 100
  Placement = pos=(0,0,0) rot=(1,0,0;1.5708rad)
  Profile = -> Sketch040
  Type = 2
FEATURE [Sketcher::SketchObject] Sketch041
  ExternalGeometry = -> [Pocket018]
  FullyConstrained = true
  MapMode = 5
  Placement = pos=(0,0,-3) rot=(0,0,1;3.14159rad)
  Support = -> [Pocket018]
  expr: Constraints[10] = <<Datos>>.anchoPlaca + <<Datos>>.tolerancia
  sketch-geometry (4):
    g0: LineSegment StartX=-1.7 StartY=37.5 StartZ=0 EndX=1.7 EndY=37.5 EndZ=0
    g1: LineSegment StartX=1.7 StartY=37.5 StartZ=0 EndX=1.7 EndY=-33 EndZ=0
    g2: LineSegment StartX=1.7 StartY=-33 StartZ=0 EndX=-1.7 EndY=-33 EndZ=0
    g3: LineSegment StartX=-1.7 StartY=-33 StartZ=0 EndX=-1.7 EndY=37.5 EndZ=0
  constraints (11):
    c: Coincident(g0,g1)
    c: Coincident(g1,g2)
    c: Coincident(g2,g3)
    c: Coincident(g3,g0)
    c: Horizontal(g2)
    c: Vertical(g1)
    c: Vertical(g3)
    c: PointOnObject(g0,g-3)
    c: PointOnObject(g1,g-4)
    c: Symmetric(g0,g0,g-2)
    c: DistanceX(g0,g0) = 3.4
FEATURE [PartDesign::Pocket] Pocket019  label="taladro_placa_ranura"
  BaseFeature = -> Pocket018
  Length = 7.1
  Length2 = 100
  Placement = pos=(0,0,0) rot=(1,0,0;1.5708rad)
  Profile = -> Sketch041
  Type = 0
FEATURE [PartDesign::Fillet] Fillet006
  Base = -> Pocket019 [Edge94,Edge55,Edge28,Edge41]
  BaseFeature = -> Pocket019
  Placement = pos=(0,0,0) rot=(1,0,0;1.5708rad)
  Radius = 1
  SupportTransform = false
FEATURE [PartDesign::Fillet] Fillet007
  Base = -> Fillet006 [Edge15,Edge93]
  BaseFeature = -> Fillet006
  Placement = pos=(0,0,0) rot=(1,0,0;1.5708rad)
  Radius = 4
  SupportTransform = false
FEATURE [PartDesign::Body] Body  label="Habitaculo_Pila"
  Group = -> [Sketch,Pad,Sketch037,Pad016,Sketch039,Pad017,Sketch040,Pocket018,Sketch041,Pocket019,Fillet006,Fillet007]
  Origin = -> Origin
  Tip = -> Fillet007
FEATURE [Sketcher::SketchObject] Sketch042
  ExternalGeometry = -> [Fillet003]
  FullyConstrained = true
  MapMode = 5
  Placement = pos=(1.4e-15,33,-8) rot=(0,0,1;0rad)
  Support = -> [Fillet003]
  expr: Constraints[10] = <<Datos>>.anchoPlaca + <<Datos>>.tolerancia
  sketch-geometry (4):
    g0: LineSegment StartX=-1.7 StartY=4 StartZ=0 EndX=1.7 EndY=4 EndZ=0
    g1: LineSegment StartX=1.7 StartY=4 StartZ=0 EndX=1.7 EndY=0 EndZ=0
    g2: LineSegment StartX=1.7 StartY=0 StartZ=0 EndX=-1.7 EndY=0 EndZ=0
    g3: LineSegment StartX=-1.7 StartY=0 StartZ=0 EndX=-1.7 EndY=4 EndZ=0
  constraints (11):
    c: Coincident(g0,g1)
    c: Coincident(g1,g2)
    c: Coincident(g2,g3)
    c: Coincident(g3,g0)
    c: Horizontal(g2)
    c: Vertical(g1)
    c: Vertical(g3)
    c: PointOnObject(g0,g-3)
    c: PointOnObject(g1,g-4)
    c: Symmetric(g0,g0,g-2)
    c: DistanceX(g0,g0) = 3.4
FEATURE [PartDesign::Pocket] Pocket020  label="Con_ranura"
  BaseFeature = -> Fillet003
  Length = 2.1
  Length2 = 100
  Placement = pos=(0,33,7e-15) rot=(0,0,1;0rad)
  Profile = -> Sketch042
  Type = 0
FEATURE [Sketcher::SketchObject] Sketch044  label="SK_algo_hundido"
  ExternalGeometry = -> [ShapeBinder006]
  FullyConstrained = true
  MapMode = 5
  Placement = pos=(0,33,7e-15) rot=(1,0,0;1.5708rad)
  Support = -> [Pocket020]
  sketch-geometry (2):
    g0: ArcOfCircle CenterX=-9 CenterY=-20.249 CenterZ=0 NormalX=0 NormalY=0 NormalZ=1 AngleXU=0 Radius=9.45 StartAngle=0.309845 EndAngle=5.97334
    g1: ArcOfCircle CenterX=9 CenterY=-20.249 CenterZ=0 NormalX=0 NormalY=0 NormalZ=1 AngleXU=0 Radius=9.45 StartAngle=3.45144 EndAngle=9.11493
  constraints (6):
    c: Coincident(g0,g-3)
    c: Coincident(g1,g-4)
    c: Diameter(g1) = 18.9
    c: Equal(g1,g0)
    c: Coincident(g1,g0)
    c: Coincident(g0,g1)
FEATURE [PartDesign::Pocket] Pocket021  label="Algo_hundido"
  BaseFeature = -> Pocket020
  Length = 1.5
  Length2 = 100
  Placement = pos=(0,33,7e-15) rot=(0,0,1;0rad)
  Profile = -> Sketch044
  Type = 0
FEATURE [PartDesign::Body] Body007  label="Tapa_Pilas"
  Group = -> [ShapeBinder006,Sketch033,Pad013,Sketch034,Pad014,Fillet003,Sketch042,Pocket020,Sketch044,Pocket021]
  Origin = -> Origin007
  Tip = -> Pocket021
FEATURE [TechDraw::DrawViewPart] View
  CoarseView = false
  Direction = (1,0,0)
  Focus = 100
  HardHidden = false
  IsoCount = 0
  IsoHidden = false
  IsoVisible = false
  LockPosition = false
  Perspective = false
  Rotation = 0
  Scale = 2
  ScaleType = 0
  SeamHidden = false
  SeamVisible = true
  SmoothHidden = false
  SmoothVisible = true
  Source = -> [Body,Body004,Body005,Body006,Body007,Body009]
  X = 149.489
  XDirection = (0,1,0)
  Y = 127.509
FEATURE [TechDraw::DrawViewDimension] Dimension
  Arbitrary = false
  ArbitraryTolerances = false
  EqualTolerance = true
  FormatSpec = %.2f
  FormatSpecOverTolerance = %+.2f
  FormatSpecUnderTolerance = %+.2f
  Inverted = false
  LockPosition = false
  MeasureType = 1
  OverTolerance = 0
  References2D = -> [View]
  Rotation = 0
  ScaleType = 0
  TheoreticalExact = false
  Type = 1
  UnderTolerance = 0
  X = 0
  Y = 55.3173
FEATURE [TechDraw::DrawViewDimension] Dimension001
  Arbitrary = false
  ArbitraryTolerances = false
  EqualTolerance = true
  FormatSpec = %.2f
  FormatSpecOverTolerance = %+.2f
  FormatSpecUnderTolerance = %+.2f
  Inverted = false
  LockPosition = false
  MeasureType = 1
  OverTolerance = 0
  References2D = -> [View]
  Rotation = 0
  ScaleType = 0
  TheoreticalExact = false
  Type = 2
  UnderTolerance = 0
  X = 121.42
  Y = -3.24005
FEATURE [TechDraw::DrawViewDimension] Dimension002
  Arbitrary = false
  ArbitraryTolerances = false
  EqualTolerance = true
  FormatSpec = %.2f
  FormatSpecOverTolerance = %+.2f
  FormatSpecUnderTolerance = %+.2f
  Inverted = false
  LockPosition = false
  MeasureType = 1
  OverTolerance = 0
  References2D = -> [View]
  Rotation = 0
  ScaleType = 0
  TheoreticalExact = false
  Type = 1
  UnderTolerance = 0
  X = -128.662
  Y = 69.0849
FEATURE [TechDraw::DrawViewDimension] Dimension003
  Arbitrary = false
  ArbitraryTolerances = false
  EqualTolerance = true
  FormatSpec = %.2f
  FormatSpecOverTolerance = %+.2f
  FormatSpecUnderTolerance = %+.2f
  Inverted = false
  LockPosition = false
  MeasureType = 1
  OverTolerance = 0
  References2D = -> [View]
  Rotation = 0
  ScaleType = 0
  TheoreticalExact = false
  Type = 1
  UnderTolerance = 0
  X = -3.18545
  Y = 4.37559
FEATURE [TechDraw::DrawPage] Page  label="Vista_general"
  KeepUpdated = true
  NextBalloonIndex = 1
  ProjectionType = 0
  Template = -> Template
  Views = -> [View,Dimension,Dimension001,Dimension002,Dimension003]
